# Revit family: 44370200(2021)
name_source: partatom
category: Plumbing Fixtures
revit_build: Autodesk Revit 2018 (Build: 20170223_1515(x64)
units: mm (PartAtom-declared; Revit-internal decimal feet)

## family parameters
Always vertical = Yes
Cut with Voids When Loaded = No
OmniClass Number = 23.45.55.00
OmniClass Title = Sanitary Faucets, Wastes
Part Type = Normal
Room Calculation Point = No
Round Connector Dimension = Use Diameter
Shared = No
Work Plane-Based = No

## types (1)
- 44370200 Overhead shower, 200x200 mm
    2D/3D/BIM Files URL = http://static.hansa.com
    3D View = https://static.hansa.com
    AssetType = Fixed
    BIMObjectName = 44370200(2021)
    Backflow Prevention EN1717 = AA
    BodyMaterial = Chrome
    Brand = HANSA
    Catalog Drawing URL = http://static.hansa.com
    Category = Shower
    CloseOffRating = 0
    Color = Chrome
    Connection = External thread;Cover plate(s)
    Connection Size = G1/2
    Dimension Drawing URL = http://static.hansa.com
    DurationUnit = Year
    EAN Number = 4057304015946
    EN Standard = EN 1111
    ETIM Class Number = EC011383 Shower head
    FDV Document URL = http://www.hansa.com
    FaucetMainMaterial = Brass
    Finish = Polished
    Flow Drawing URL = http://static.hansa.com
    Flow Rate At 300kPa = 0.3 L/s
    Flow Rate At 300kPa With Flow Controller = 0.2 L/s
    FlowCoefficient = 0
    Group = Overhead shower
    IfcExportAs = IfcValveType
    IfcExportType = FAUCET
    InletConnectionSize = 10 mm  [stored 0.0328084 ft]
    Installation Type = Ceiling mounted
    Installation and Maintenance Guide URL = http://static.hansa.com
    Interactive AR View URL = https://static.hansa.com
    Manufacturer = HANSA
    ManufacturerName = HANSA
    ManufacturerURL = http://www.hansa.com
    Market = International;Germany;Austria;Switzerland;Belgium;Netherlands;France;Czech Republic;Slovakia;Hungary;Romania;Italy;Spain;Greece;Portugal;Australia
    Material = Chrome
    Max. Hot Water Supply = 65 °C
    Mobile Product Information URL = http://mpi.hansa.com
    Model = 44370200 Overhead shower, 200x200 mm
    ModelReference = 44370200
    NBSDescription = Shower heads
    NBSReference = 45-35-70/333
    Name = 44370200 Overhead shower, 200x200 mm
    Name_en = 44370200 Overhead shower, 200x200 mm
    Noise Class = I (ISO 3822)
    NominalDepth = 200 mm  [stored 0.656168 ft]
    NominalHeight = 256 mm
    NominalWidth = 200 mm  [stored 0.656168 ft]
    Over Head Shower Size = 200x200 mm
    PackageWeight = 0.75 kg
    Product Code = 44370200
    Product Family = HANSABASICJET Style
    Product Image URL = http://static.hansa.com
    Product URL = http://static.hansa.com
    Revision = 1
    Sales Package dimensions (LxWxH) = 371 x 203 x 105
    Shape = Sculptured
    Shower Parts = Overhead shower;Rotatable ball joint connection;Anti limescale technology (easy to clean)
    Shower Spray = Rain
    Shower Spray Number = 1 shower spray
    Size = 200x200x256 mm
    Spare-Part Information URL = http://static.hansa.com
    Surface treatment = Chrome
    Technical DataSheet URL = http://www.hansa.com
    UNSPSC Class Number = 30181801 Shower head
    URL Declaration of Conformity = http://static.hansa.com
    URL REACH = http://static.hansa.com
    Uniclass2 = Pr_40_30_96_76
    Uniclass2015Description = Shower heads
    Uniclass2015Reference = Pr_40_20_87_76
    Version = 2
    VersionDate = 01/07/2022
    Warranty Information URL = http://warranty.hansa.com
    WarrantyDescription = http://warranty.hansa.com
    WarrantyDurationUnit = Year
    Working Pressure = 100 - 1000 kPa
    WorkingPressure = 100 - 1000 kPa

note: [stored X ft] marks values corroborated as IEEE doubles in the binary element streams (Revit-internal decimal feet)

## geometry (parser evidence)
native form markers: Sweep x6
no freeform markers — native parametric forms only
